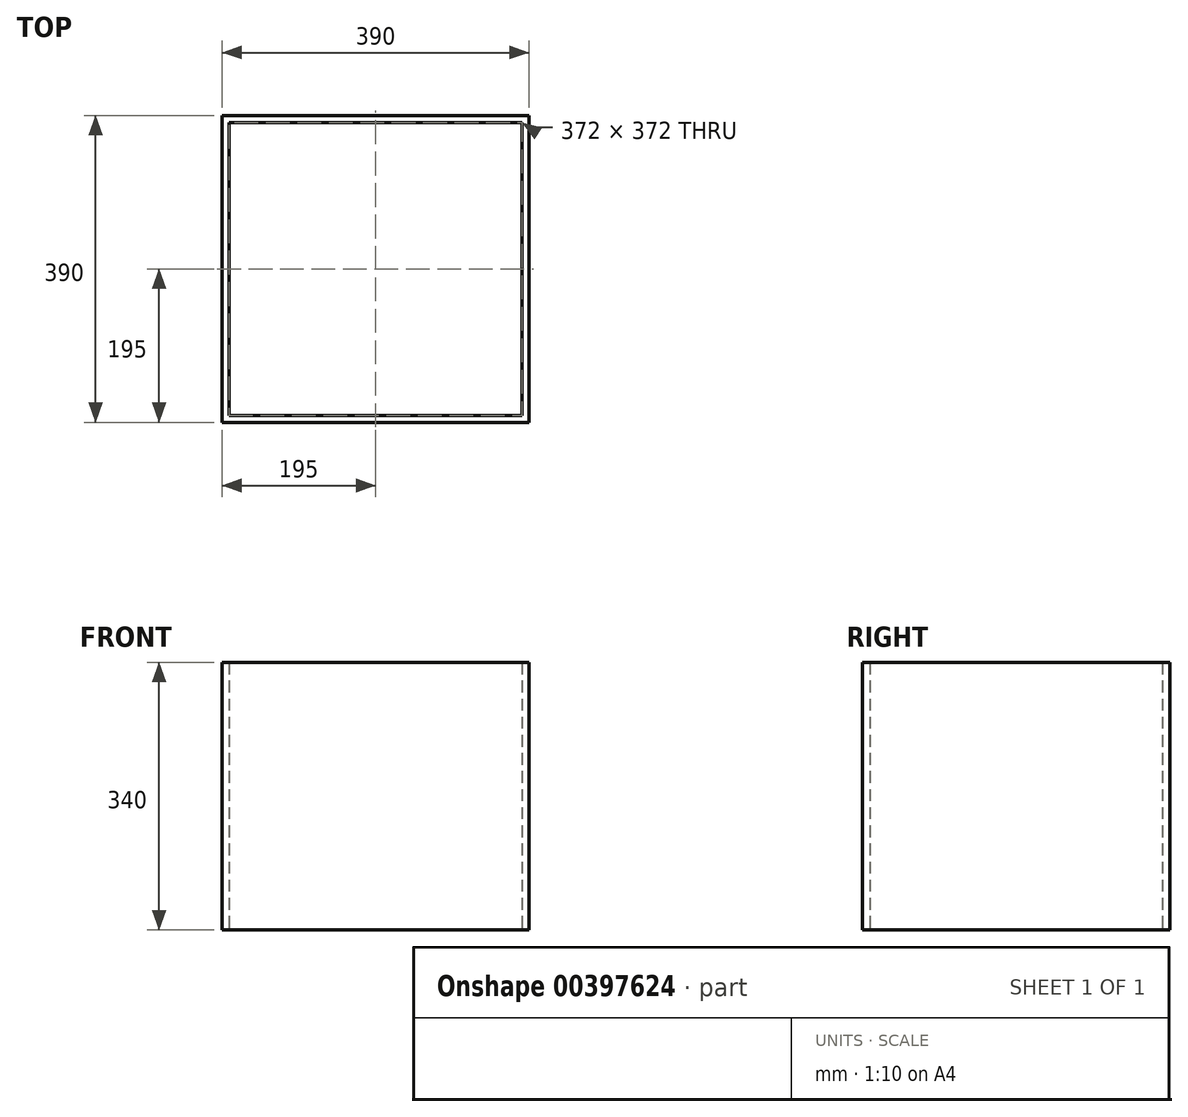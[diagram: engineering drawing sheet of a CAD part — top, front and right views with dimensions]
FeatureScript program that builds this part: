
annotation { "Feature Type Name" : "Feature", "Feature Type Description" : "" }
export const myFeature = defineFeature(function(context is Context, id is Id, definition is map)
    precondition{}
    {
        {
            var Q0;
            Q0=qCreatedBy(makeId("Top.planeOp"),FACE);
            var sketch = newSketch(context, id + "F0", { "sketchPlane" : qUnion([Q0])});
            skLineSegment(sketch, "E0.bottom", {"start": v(0, 0) * mm, "end": v(390, 0) * mm});
            skLineSegment(sketch, "E0.top", {"start": v(0, 390) * mm, "end": v(390, 390) * mm});
            skLineSegment(sketch, "E0.left", {"start": v(0, 0) * mm, "end": v(0, 390) * mm});
            skLineSegment(sketch, "E0.right", {"start": v(390, 0) * mm, "end": v(390, 390) * mm});
            skLineSegment(sketch, "E1.bottom", {"start": v(9, 9) * mm, "end": v(381, 9) * mm});
            skLineSegment(sketch, "E1.top", {"start": v(9, 381) * mm, "end": v(381, 381) * mm});
            skLineSegment(sketch, "E1.left", {"start": v(9, 9) * mm, "end": v(9, 381) * mm});
            skLineSegment(sketch, "E1.right", {"start": v(381, 9) * mm, "end": v(381, 381) * mm});
            skSolve(sketch);
        }
        {
            var Q0;
            Q0 = qSketchRegion(id + "F0", true);
            extrude(context, id + "F1", {"entities" : qUnion([Q0]), "depth" : 340 * mm});
        }
    });
